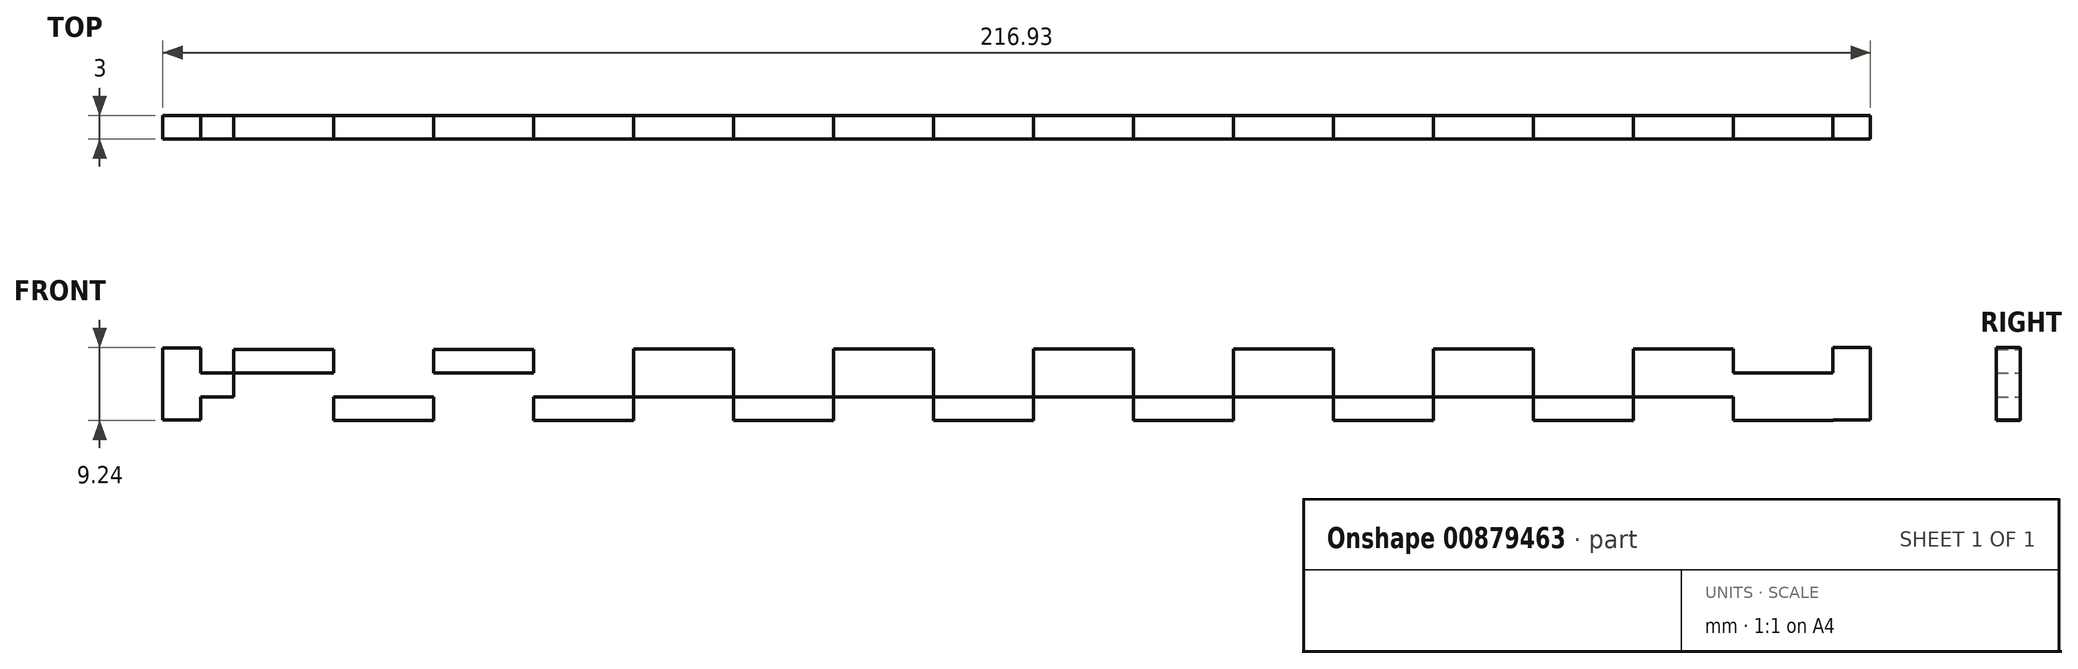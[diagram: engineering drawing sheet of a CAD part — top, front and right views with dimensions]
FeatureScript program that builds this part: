
annotation { "Feature Type Name" : "Feature", "Feature Type Description" : "" }
export const myFeature = defineFeature(function(context is Context, id is Id, definition is map)
    precondition{}
    {
        {
            var Q0;
            Q0=qCreatedBy(makeId("Front.planeOp"),FACE);
            var sketch = newSketch(context, id + "F0", { "sketchPlane" : qUnion([Q0])});
            skLineSegment(sketch, "E0.bottom", {"start": v(-108.46, 1.5) * mm, "end": v(108.46, 1.5) * mm});
            skLineSegment(sketch, "E0.top", {"start": v(-108.46, -1.5) * mm, "end": v(108.46, -1.5) * mm});
            skLineSegment(sketch, "E0.left", {"start": v(-108.46, 1.5) * mm, "end": v(-108.46, -1.5) * mm});
            skLineSegment(sketch, "E0.right", {"start": v(108.46, 1.5) * mm, "end": v(108.46, -1.5) * mm});
            skPoint(sketch, "E0.middle", {"position": v(0, 0) * mm});
            skPoint(sketch, "E1", {"position": v(-86.76, 1.5) * mm});
            skLineSegment(sketch, "E2.bottom", {"start": v(-86.76, 1.5) * mm, "end": v(-74.06, 1.5) * mm});
            skLineSegment(sketch, "E2.top", {"start": v(-86.76, -4.5) * mm, "end": v(-74.06, -4.5) * mm});
            skLineSegment(sketch, "E2.left", {"start": v(-86.76, 1.5) * mm, "end": v(-86.76, -4.5) * mm});
            skLineSegment(sketch, "E2.right", {"start": v(-74.06, 1.5) * mm, "end": v(-74.06, -4.5) * mm});
            skPoint(sketch, "E3", {"position": v(-80.4, 1.5) * mm});
            skLineSegment(sketch, "E4.1.0.0", {"start": v(-61.36, 1.5) * mm, "end": v(-48.66, 1.5) * mm});
            skLineSegment(sketch, "E4.1.0.1", {"start": v(-61.36, 1.5) * mm, "end": v(-61.36, -4.5) * mm});
            skLineSegment(sketch, "E4.1.0.2", {"start": v(-61.36, -4.5) * mm, "end": v(-48.66, -4.5) * mm});
            skPoint(sketch, "E4.1.0.3", {"position": v(-61.36, 1.5) * mm});
            skLineSegment(sketch, "E4.1.0.4", {"start": v(-48.66, 1.5) * mm, "end": v(-48.66, -4.5) * mm});
            skPoint(sketch, "E4.1.0.5", {"position": v(-55, 1.5) * mm});
            skLineSegment(sketch, "E4.2.0.0", {"start": v(-35.96, 1.5) * mm, "end": v(-23.26, 1.5) * mm});
            skLineSegment(sketch, "E4.2.0.1", {"start": v(-35.96, 1.5) * mm, "end": v(-35.96, -4.5) * mm});
            skLineSegment(sketch, "E4.2.0.2", {"start": v(-35.96, -4.5) * mm, "end": v(-23.26, -4.5) * mm});
            skPoint(sketch, "E4.2.0.3", {"position": v(-35.96, 1.5) * mm});
            skLineSegment(sketch, "E4.2.0.4", {"start": v(-23.26, 1.5) * mm, "end": v(-23.26, -4.5) * mm});
            skPoint(sketch, "E4.2.0.5", {"position": v(-29.6, 1.5) * mm});
            skLineSegment(sketch, "E4.3.0.0", {"start": v(-10.56, 1.5) * mm, "end": v(2.14, 1.5) * mm});
            skLineSegment(sketch, "E4.3.0.1", {"start": v(-10.56, 1.5) * mm, "end": v(-10.56, -4.5) * mm});
            skLineSegment(sketch, "E4.3.0.2", {"start": v(-10.56, -4.5) * mm, "end": v(2.14, -4.5) * mm});
            skPoint(sketch, "E4.3.0.3", {"position": v(-10.56, 1.5) * mm});
            skLineSegment(sketch, "E4.3.0.4", {"start": v(2.14, 1.5) * mm, "end": v(2.14, -4.5) * mm});
            skPoint(sketch, "E4.3.0.5", {"position": v(-4.2, 1.5) * mm});
            skLineSegment(sketch, "E4.4.0.0", {"start": v(14.84, 1.5) * mm, "end": v(27.54, 1.5) * mm});
            skLineSegment(sketch, "E4.4.0.1", {"start": v(14.84, 1.5) * mm, "end": v(14.84, -4.5) * mm});
            skLineSegment(sketch, "E4.4.0.2", {"start": v(14.84, -4.5) * mm, "end": v(27.54, -4.5) * mm});
            skPoint(sketch, "E4.4.0.3", {"position": v(14.84, 1.5) * mm});
            skLineSegment(sketch, "E4.4.0.4", {"start": v(27.54, 1.5) * mm, "end": v(27.54, -4.5) * mm});
            skPoint(sketch, "E4.4.0.5", {"position": v(21.2, 1.5) * mm});
            skLineSegment(sketch, "E4.5.0.0", {"start": v(40.24, 1.5) * mm, "end": v(52.94, 1.5) * mm});
            skLineSegment(sketch, "E4.5.0.1", {"start": v(40.24, 1.5) * mm, "end": v(40.24, -4.5) * mm});
            skLineSegment(sketch, "E4.5.0.2", {"start": v(40.24, -4.5) * mm, "end": v(52.94, -4.5) * mm});
            skPoint(sketch, "E4.5.0.3", {"position": v(40.24, 1.5) * mm});
            skLineSegment(sketch, "E4.5.0.4", {"start": v(52.94, 1.5) * mm, "end": v(52.94, -4.5) * mm});
            skPoint(sketch, "E4.5.0.5", {"position": v(46.6, 1.5) * mm});
            skLineSegment(sketch, "E4.6.0.0", {"start": v(65.64, 1.5) * mm, "end": v(78.34, 1.5) * mm});
            skLineSegment(sketch, "E4.6.0.1", {"start": v(65.64, 1.5) * mm, "end": v(65.64, -4.5) * mm});
            skLineSegment(sketch, "E4.6.0.2", {"start": v(65.64, -4.5) * mm, "end": v(78.34, -4.5) * mm});
            skPoint(sketch, "E4.6.0.3", {"position": v(65.64, 1.5) * mm});
            skLineSegment(sketch, "E4.6.0.4", {"start": v(78.34, 1.5) * mm, "end": v(78.34, -4.5) * mm});
            skPoint(sketch, "E4.6.0.5", {"position": v(72, 1.5) * mm});
            skLineSegment(sketch, "E4.7.0.0", {"start": v(91.04, 1.5) * mm, "end": v(103.74, 1.5) * mm});
            skLineSegment(sketch, "E4.7.0.1", {"start": v(91.04, 1.5) * mm, "end": v(91.04, -4.5) * mm});
            skLineSegment(sketch, "E4.7.0.2", {"start": v(91.04, -4.5) * mm, "end": v(103.74, -4.5) * mm});
            skPoint(sketch, "E4.7.0.3", {"position": v(91.04, 1.5) * mm});
            skLineSegment(sketch, "E4.7.0.4", {"start": v(103.74, 1.5) * mm, "end": v(103.74, -4.5) * mm});
            skPoint(sketch, "E4.7.0.5", {"position": v(97.4, 1.5) * mm});
            skLineSegment(sketch, "E4.direction1", {"start": v(-86.76, -4.5) * mm, "end": v(-61.36, -4.5) * mm, "construction": true});
            skLineSegment(sketch, "E5.bottom", {"start": v(-103.66, 4.71) * mm, "end": v(-108.46, 4.71) * mm});
            skLineSegment(sketch, "E5.top", {"start": v(-103.66, -4.46) * mm, "end": v(-108.46, -4.46) * mm});
            skLineSegment(sketch, "E5.left", {"start": v(-103.66, 4.71) * mm, "end": v(-103.66, -4.46) * mm});
            skLineSegment(sketch, "E5.right", {"start": v(-108.46, 4.71) * mm, "end": v(-108.46, -4.46) * mm});
            skLineSegment(sketch, "E6.bottom", {"start": v(108.47, 4.74) * mm, "end": v(103.67, 4.74) * mm});
            skLineSegment(sketch, "E6.top", {"start": v(108.47, -4.43) * mm, "end": v(103.67, -4.43) * mm});
            skLineSegment(sketch, "E6.left", {"start": v(108.47, 4.74) * mm, "end": v(108.47, -4.43) * mm});
            skLineSegment(sketch, "E6.right", {"start": v(103.67, 4.74) * mm, "end": v(103.67, -4.43) * mm});
            skLineSegment(sketch, "E7.bottom", {"start": v(-86.76, -1.5) * mm, "end": v(-99.46, -1.5) * mm});
            skLineSegment(sketch, "E7.top", {"start": v(-86.76, 4.5) * mm, "end": v(-99.46, 4.5) * mm});
            skLineSegment(sketch, "E7.left", {"start": v(-86.76, -1.5) * mm, "end": v(-86.76, 4.5) * mm});
            skLineSegment(sketch, "E7.right", {"start": v(-99.46, -1.5) * mm, "end": v(-99.46, 4.5) * mm});
            skPoint(sketch, "E8.1.0.0", {"position": v(-61.36, 1.59) * mm});
            skLineSegment(sketch, "E8.1.0.1", {"start": v(-61.36, 4.5) * mm, "end": v(-74.06, 4.5) * mm});
            skLineSegment(sketch, "E8.1.0.2", {"start": v(-61.36, -1.5) * mm, "end": v(-61.36, 4.5) * mm});
            skLineSegment(sketch, "E8.1.0.3", {"start": v(-74.06, -1.5) * mm, "end": v(-74.06, 4.5) * mm});
            skLineSegment(sketch, "E8.1.0.4", {"start": v(-61.36, -1.5) * mm, "end": v(-74.06, -1.5) * mm});
            skPoint(sketch, "E8.2.0.0", {"position": v(-35.96, 1.59) * mm});
            skLineSegment(sketch, "E8.2.0.1", {"start": v(-35.96, 4.59) * mm, "end": v(-48.66, 4.59) * mm});
            skLineSegment(sketch, "E8.2.0.2", {"start": v(-35.96, -1.41) * mm, "end": v(-35.96, 4.59) * mm});
            skLineSegment(sketch, "E8.2.0.3", {"start": v(-48.66, -1.41) * mm, "end": v(-48.66, 4.59) * mm});
            skLineSegment(sketch, "E8.2.0.4", {"start": v(-35.96, -1.41) * mm, "end": v(-48.66, -1.41) * mm});
            skPoint(sketch, "E8.3.0.0", {"position": v(-10.56, 1.59) * mm});
            skLineSegment(sketch, "E8.3.0.1", {"start": v(-10.56, 4.59) * mm, "end": v(-23.26, 4.59) * mm});
            skLineSegment(sketch, "E8.3.0.2", {"start": v(-10.56, -1.41) * mm, "end": v(-10.56, 4.59) * mm});
            skLineSegment(sketch, "E8.3.0.3", {"start": v(-23.26, -1.41) * mm, "end": v(-23.26, 4.59) * mm});
            skLineSegment(sketch, "E8.3.0.4", {"start": v(-10.56, -1.41) * mm, "end": v(-23.26, -1.41) * mm});
            skPoint(sketch, "E8.4.0.0", {"position": v(14.84, 1.59) * mm});
            skLineSegment(sketch, "E8.4.0.1", {"start": v(14.84, 4.59) * mm, "end": v(2.14, 4.59) * mm});
            skLineSegment(sketch, "E8.4.0.2", {"start": v(14.84, -1.41) * mm, "end": v(14.84, 4.59) * mm});
            skLineSegment(sketch, "E8.4.0.3", {"start": v(2.14, -1.41) * mm, "end": v(2.14, 4.59) * mm});
            skLineSegment(sketch, "E8.4.0.4", {"start": v(14.84, -1.41) * mm, "end": v(2.14, -1.41) * mm});
            skPoint(sketch, "E8.5.0.0", {"position": v(40.24, 1.59) * mm});
            skLineSegment(sketch, "E8.5.0.1", {"start": v(40.24, 4.59) * mm, "end": v(27.54, 4.59) * mm});
            skLineSegment(sketch, "E8.5.0.2", {"start": v(40.24, -1.41) * mm, "end": v(40.24, 4.59) * mm});
            skLineSegment(sketch, "E8.5.0.3", {"start": v(27.54, -1.41) * mm, "end": v(27.54, 4.59) * mm});
            skLineSegment(sketch, "E8.5.0.4", {"start": v(40.24, -1.41) * mm, "end": v(27.54, -1.41) * mm});
            skPoint(sketch, "E8.6.0.0", {"position": v(65.64, 1.59) * mm});
            skLineSegment(sketch, "E8.6.0.1", {"start": v(65.64, 4.59) * mm, "end": v(52.94, 4.59) * mm});
            skLineSegment(sketch, "E8.6.0.2", {"start": v(65.64, -1.41) * mm, "end": v(65.64, 4.59) * mm});
            skLineSegment(sketch, "E8.6.0.3", {"start": v(52.94, -1.41) * mm, "end": v(52.94, 4.59) * mm});
            skLineSegment(sketch, "E8.6.0.4", {"start": v(65.64, -1.41) * mm, "end": v(52.94, -1.41) * mm});
            skPoint(sketch, "E8.7.0.0", {"position": v(91.04, 1.59) * mm});
            skLineSegment(sketch, "E8.7.0.1", {"start": v(91.04, 4.59) * mm, "end": v(78.34, 4.59) * mm});
            skLineSegment(sketch, "E8.7.0.2", {"start": v(91.04, -1.41) * mm, "end": v(91.04, 4.59) * mm});
            skLineSegment(sketch, "E8.7.0.3", {"start": v(78.34, -1.41) * mm, "end": v(78.34, 4.59) * mm});
            skLineSegment(sketch, "E8.7.0.4", {"start": v(91.04, -1.41) * mm, "end": v(78.34, -1.41) * mm});
            skLineSegment(sketch, "E8.direction1", {"start": v(-99.46, -1.5) * mm, "end": v(-74.06, -1.5) * mm, "construction": true});
            skSolve(sketch);
        }
        {
            var Q0;
            {var subQ5=sQuery(id+"F0.wireOp",EDGE,"E8.7.0.1");Q0=makeQuery(id+"F0.imprint","IMPRINT",FACE,{"disambiguationData":[TD([[makeQuery(id+"F0.imprint","IMPRINT",EDGE,{"derivedFrom":subQ5}),1.0]])]});}
            var Q1;
            {var subQ5=sQuery(id+"F0.wireOp",EDGE,"E8.5.0.1");Q1=makeQuery(id+"F0.imprint","IMPRINT",FACE,{"disambiguationData":[TD([[makeQuery(id+"F0.imprint","IMPRINT",EDGE,{"derivedFrom":subQ5}),1.0]])]});}
            var Q2;
            {var subQ5=sQuery(id+"F0.wireOp",EDGE,"E8.3.0.1");Q2=makeQuery(id+"F0.imprint","IMPRINT",FACE,{"disambiguationData":[TD([[makeQuery(id+"F0.imprint","IMPRINT",EDGE,{"derivedFrom":subQ5}),1.0]])]});}
            var Q3;
            {var subQ5=sQuery(id+"F0.wireOp",EDGE,"E8.2.0.1");Q3=makeQuery(id+"F0.imprint","IMPRINT",FACE,{"disambiguationData":[TD([[makeQuery(id+"F0.imprint","IMPRINT",EDGE,{"derivedFrom":subQ5}),1.0]])]});}
            var Q4;
            {var subQ5=sQuery(id+"F0.wireOp",EDGE,"E8.1.0.1");Q4=makeQuery(id+"F0.imprint","IMPRINT",FACE,{"disambiguationData":[TD([[makeQuery(id+"F0.imprint","IMPRINT",EDGE,{"derivedFrom":subQ5}),1.0]])]});}
            var Q5;
            {var subQ5=sQuery(id+"F0.wireOp",EDGE,"E8.6.0.1");Q5=makeQuery(id+"F0.imprint","IMPRINT",FACE,{"disambiguationData":[TD([[makeQuery(id+"F0.imprint","IMPRINT",EDGE,{"derivedFrom":subQ5}),1.0]])]});}
            var Q6;
            {var subQ5=sQuery(id+"F0.wireOp",EDGE,"E7.bottom");Q6=makeQuery(id+"F0.imprint","IMPRINT",FACE,{"disambiguationData":[TD([[makeQuery(id+"F0.imprint","IMPRINT",EDGE,{"derivedFrom":subQ5}),-1.0]])]});}
            var Q7;
            {var subQ5=sQuery(id+"F0.wireOp",EDGE,"E7.top");Q7=makeQuery(id+"F0.imprint","IMPRINT",FACE,{"disambiguationData":[TD([[makeQuery(id+"F0.imprint","IMPRINT",EDGE,{"derivedFrom":subQ5}),1.0]])]});}
            var Q8;
            {var subQ5=sQuery(id+"F0.wireOp",EDGE,"E8.7.0.4");Q8=makeQuery(id+"F0.imprint","IMPRINT",FACE,{"disambiguationData":[TD([[makeQuery(id+"F0.imprint","IMPRINT",EDGE,{"derivedFrom":subQ5}),-1.0]])]});}
            var Q9;
            {var subQ0=sQuery(id+"F0.wireOp",EDGE,"E4.1.0.1");Q9=makeQuery(id+"F0.imprint","IMPRINT",FACE,{"disambiguationData":[TD([[makeQuery(id+"F0.imprint","IMPRINT",EDGE,{"derivedFrom":subQ0}),1.0]])]});}
            var Q10;
            {var subQ5=sQuery(id+"F0.wireOp",EDGE,"E8.2.0.4");Q10=makeQuery(id+"F0.imprint","IMPRINT",FACE,{"disambiguationData":[TD([[makeQuery(id+"F0.imprint","IMPRINT",EDGE,{"derivedFrom":subQ5}),1.0]])]});}
            var Q11;
            {var subQ5=sQuery(id+"F0.wireOp",EDGE,"E2.bottom");Q11=makeQuery(id+"F0.imprint","IMPRINT",FACE,{"disambiguationData":[TD([[makeQuery(id+"F0.imprint","IMPRINT",EDGE,{"derivedFrom":subQ5}),-1.0]])]});}
            var Q12;
            {var subQ5=sQuery(id+"F0.wireOp",EDGE,"E4.5.0.2");Q12=makeQuery(id+"F0.imprint","IMPRINT",FACE,{"disambiguationData":[TD([[makeQuery(id+"F0.imprint","IMPRINT",EDGE,{"derivedFrom":subQ5}),1.0]])]});}
            var Q13;
            Q13=makeQuery(id+"F0.imprint","IMPRINT",FACE,{"disambiguationData":[TD([[makeQuery(id+"F0.imprint","IMPRINT",EDGE,{"derivedFrom":sQuery(id+"F0.wireOp",EDGE,"E2.top")}),1.0]])]});
            var Q14;
            {var subQ9=sQuery(id+"F0.wireOp",EDGE,"E4.5.0.0");Q14=makeQuery(id+"F0.imprint","IMPRINT",FACE,{"disambiguationData":[TD([[makeQuery(id+"F0.imprint","IMPRINT",EDGE,{"derivedFrom":subQ9}),-1.0]])]});}
            var Q15;
            {var subQ5=sQuery(id+"F0.wireOp",EDGE,"E8.2.0.4");Q15=makeQuery(id+"F0.imprint","IMPRINT",FACE,{"disambiguationData":[TD([[makeQuery(id+"F0.imprint","IMPRINT",EDGE,{"derivedFrom":subQ5}),-1.0]])]});}
            var Q16;
            {var subQ5=sQuery(id+"F0.wireOp",EDGE,"E8.6.0.4");Q16=makeQuery(id+"F0.imprint","IMPRINT",FACE,{"disambiguationData":[TD([[makeQuery(id+"F0.imprint","IMPRINT",EDGE,{"derivedFrom":subQ5}),-1.0]])]});}
            var Q17;
            {var subQ5=sQuery(id+"F0.wireOp",EDGE,"E8.3.0.4");Q17=makeQuery(id+"F0.imprint","IMPRINT",FACE,{"disambiguationData":[TD([[makeQuery(id+"F0.imprint","IMPRINT",EDGE,{"derivedFrom":subQ5}),1.0]])]});}
            var Q18;
            {var subQ6=sQuery(id+"F0.wireOp",EDGE,"E4.1.0.0");Q18=makeQuery(id+"F0.imprint","IMPRINT",FACE,{"disambiguationData":[TD([[makeQuery(id+"F0.imprint","IMPRINT",EDGE,{"derivedFrom":subQ6}),-1.0]])]});}
            var Q19;
            {var subQ5=sQuery(id+"F0.wireOp",EDGE,"E4.6.0.0");Q19=makeQuery(id+"F0.imprint","IMPRINT",FACE,{"disambiguationData":[TD([[makeQuery(id+"F0.imprint","IMPRINT",EDGE,{"derivedFrom":subQ5}),-1.0]])]});}
            var Q20;
            {var subQ3=sQuery(id+"F0.wireOp",EDGE,"E0.top");var subQ7=sQuery(id+"F0.wireOp",EDGE,"E4.7.0.1");var subQ9=makeQuery(id+"F0.imprint","INTERSECT",VERTEX,{"derivedFrom":[subQ3,subQ7]});Q20=makeQuery(id+"F0.imprint","IMPRINT",FACE,{"disambiguationData":[TD([[makeQuery(id+"F0.imprint","IMPRINT",EDGE,{"disambiguationData":[TD([[subQ9,-1.0]])],"derivedFrom":subQ3}),1.0]])]});}
            var Q21;
            {var subQ5=sQuery(id+"F0.wireOp",EDGE,"E4.6.0.2");Q21=makeQuery(id+"F0.imprint","IMPRINT",FACE,{"disambiguationData":[TD([[makeQuery(id+"F0.imprint","IMPRINT",EDGE,{"derivedFrom":subQ5}),1.0]])]});}
            var Q22;
            {var subQ0=sQuery(id+"F0.wireOp",EDGE,"E4.7.0.2");Q22=makeQuery(id+"F0.imprint","IMPRINT",FACE,{"disambiguationData":[TD([[makeQuery(id+"F0.imprint","IMPRINT",EDGE,{"derivedFrom":subQ0}),1.0]])]});}
            var Q23;
            {var subQ5=sQuery(id+"F0.wireOp",EDGE,"E4.4.0.2");Q23=makeQuery(id+"F0.imprint","IMPRINT",FACE,{"disambiguationData":[TD([[makeQuery(id+"F0.imprint","IMPRINT",EDGE,{"derivedFrom":subQ5}),1.0]])]});}
            var Q24;
            {var subQ5=sQuery(id+"F0.wireOp",EDGE,"E8.4.0.4");Q24=makeQuery(id+"F0.imprint","IMPRINT",FACE,{"disambiguationData":[TD([[makeQuery(id+"F0.imprint","IMPRINT",EDGE,{"derivedFrom":subQ5}),1.0]])]});}
            var Q25;
            {var subQ5=sQuery(id+"F0.wireOp",EDGE,"E8.7.0.4");Q25=makeQuery(id+"F0.imprint","IMPRINT",FACE,{"disambiguationData":[TD([[makeQuery(id+"F0.imprint","IMPRINT",EDGE,{"derivedFrom":subQ5}),1.0]])]});}
            var Q26;
            {var subQ5=sQuery(id+"F0.wireOp",EDGE,"E4.4.0.0");Q26=makeQuery(id+"F0.imprint","IMPRINT",FACE,{"disambiguationData":[TD([[makeQuery(id+"F0.imprint","IMPRINT",EDGE,{"derivedFrom":subQ5}),-1.0]])]});}
            var Q27;
            {var subQ5=sQuery(id+"F0.wireOp",EDGE,"E8.5.0.4");Q27=makeQuery(id+"F0.imprint","IMPRINT",FACE,{"disambiguationData":[TD([[makeQuery(id+"F0.imprint","IMPRINT",EDGE,{"derivedFrom":subQ5}),-1.0]])]});}
            var Q28;
            {var subQ5=sQuery(id+"F0.wireOp",EDGE,"E8.4.0.4");Q28=makeQuery(id+"F0.imprint","IMPRINT",FACE,{"disambiguationData":[TD([[makeQuery(id+"F0.imprint","IMPRINT",EDGE,{"derivedFrom":subQ5}),-1.0]])]});}
            var Q29;
            {var subQ9=sQuery(id+"F0.wireOp",EDGE,"E4.2.0.0");Q29=makeQuery(id+"F0.imprint","IMPRINT",FACE,{"disambiguationData":[TD([[makeQuery(id+"F0.imprint","IMPRINT",EDGE,{"derivedFrom":subQ9}),-1.0]])]});}
            var Q30;
            {var subQ5=sQuery(id+"F0.wireOp",EDGE,"E8.6.0.4");Q30=makeQuery(id+"F0.imprint","IMPRINT",FACE,{"disambiguationData":[TD([[makeQuery(id+"F0.imprint","IMPRINT",EDGE,{"derivedFrom":subQ5}),1.0]])]});}
            var Q31;
            {var subQ5=sQuery(id+"F0.wireOp",EDGE,"E4.2.0.2");Q31=makeQuery(id+"F0.imprint","IMPRINT",FACE,{"disambiguationData":[TD([[makeQuery(id+"F0.imprint","IMPRINT",EDGE,{"derivedFrom":subQ5}),1.0]])]});}
            var Q32;
            {var subQ5=sQuery(id+"F0.wireOp",EDGE,"E8.4.0.1");Q32=makeQuery(id+"F0.imprint","IMPRINT",FACE,{"disambiguationData":[TD([[makeQuery(id+"F0.imprint","IMPRINT",EDGE,{"derivedFrom":subQ5}),1.0]])]});}
            var Q33;
            {var subQ5=sQuery(id+"F0.wireOp",EDGE,"E8.3.0.4");Q33=makeQuery(id+"F0.imprint","IMPRINT",FACE,{"disambiguationData":[TD([[makeQuery(id+"F0.imprint","IMPRINT",EDGE,{"derivedFrom":subQ5}),-1.0]])]});}
            var Q34;
            {var subQ5=sQuery(id+"F0.wireOp",EDGE,"E8.1.0.4");Q34=makeQuery(id+"F0.imprint","IMPRINT",FACE,{"disambiguationData":[TD([[makeQuery(id+"F0.imprint","IMPRINT",EDGE,{"derivedFrom":subQ5}),-1.0]])]});}
            var Q35;
            {var subQ5=sQuery(id+"F0.wireOp",EDGE,"E8.5.0.4");Q35=makeQuery(id+"F0.imprint","IMPRINT",FACE,{"disambiguationData":[TD([[makeQuery(id+"F0.imprint","IMPRINT",EDGE,{"derivedFrom":subQ5}),1.0]])]});}
            var Q36;
            {var subQ0=sQuery(id+"F0.wireOp",EDGE,"E5.right");var subQ1=sQuery(id+"F0.wireOp",EDGE,"E0.bottom");var subQ2=makeQuery(id+"F0.imprint","INTERSECT",VERTEX,{"derivedFrom":[subQ1,subQ0]});Q36=makeQuery(id+"F0.imprint","IMPRINT",FACE,{"disambiguationData":[TD([[makeQuery(id+"F0.imprint","IMPRINT",EDGE,{"disambiguationData":[TD([[subQ2,-1.0]])],"derivedFrom":subQ1}),-1.0]])]});}
            var Q37;
            {var subQ5=sQuery(id+"F0.wireOp",EDGE,"E5.top");Q37=makeQuery(id+"F0.imprint","IMPRINT",FACE,{"disambiguationData":[TD([[makeQuery(id+"F0.imprint","IMPRINT",EDGE,{"derivedFrom":subQ5}),-1.0]])]});}
            var Q38;
            {var subQ5=sQuery(id+"F0.wireOp",EDGE,"E4.3.0.2");Q38=makeQuery(id+"F0.imprint","IMPRINT",FACE,{"disambiguationData":[TD([[makeQuery(id+"F0.imprint","IMPRINT",EDGE,{"derivedFrom":subQ5}),1.0]])]});}
            var Q39;
            {var subQ0=sQuery(id+"F0.wireOp",EDGE,"E5.left");var subQ1=sQuery(id+"F0.wireOp",EDGE,"E0.bottom");var subQ2=makeQuery(id+"F0.imprint","INTERSECT",VERTEX,{"derivedFrom":[subQ1,subQ0]});Q39=makeQuery(id+"F0.imprint","IMPRINT",FACE,{"disambiguationData":[TD([[makeQuery(id+"F0.imprint","IMPRINT",EDGE,{"disambiguationData":[TD([[subQ2,-1.0]])],"derivedFrom":subQ1}),-1.0]])]});}
            var Q40;
            {var subQ9=sQuery(id+"F0.wireOp",EDGE,"E4.3.0.0");Q40=makeQuery(id+"F0.imprint","IMPRINT",FACE,{"disambiguationData":[TD([[makeQuery(id+"F0.imprint","IMPRINT",EDGE,{"derivedFrom":subQ9}),-1.0]])]});}
            var Q41;
            {var subQ5=sQuery(id+"F0.wireOp",EDGE,"E5.bottom");Q41=makeQuery(id+"F0.imprint","IMPRINT",FACE,{"disambiguationData":[TD([[makeQuery(id+"F0.imprint","IMPRINT",EDGE,{"derivedFrom":subQ5}),1.0]])]});}
            var Q42;
            {var subQ0=sQuery(id+"F0.wireOp",EDGE,"E0.right");Q42=makeQuery(id+"F0.imprint","IMPRINT",FACE,{"disambiguationData":[TD([[makeQuery(id+"F0.imprint","IMPRINT",EDGE,{"derivedFrom":subQ0}),1.0]])]});}
            var Q43;
            {var subQ0=sQuery(id+"F0.wireOp",EDGE,"E0.right");Q43=makeQuery(id+"F0.imprint","IMPRINT",FACE,{"disambiguationData":[TD([[makeQuery(id+"F0.imprint","IMPRINT",EDGE,{"derivedFrom":subQ0}),-1.0]])]});}
            var Q44;
            {var subQ0=sQuery(id+"F0.wireOp",EDGE,"E6.right");var subQ1=sQuery(id+"F0.wireOp",EDGE,"E0.top");var subQ2=makeQuery(id+"F0.imprint","INTERSECT",VERTEX,{"derivedFrom":[subQ1,subQ0]});Q44=makeQuery(id+"F0.imprint","IMPRINT",FACE,{"disambiguationData":[TD([[makeQuery(id+"F0.imprint","IMPRINT",EDGE,{"disambiguationData":[TD([[subQ2,-1.0]])],"derivedFrom":subQ1}),1.0]])]});}
            var Q45;
            {var subQ0=sQuery(id+"F0.wireOp",EDGE,"E6.right");var subQ1=sQuery(id+"F0.wireOp",EDGE,"E0.top");var subQ2=makeQuery(id+"F0.imprint","INTERSECT",VERTEX,{"derivedFrom":[subQ1,subQ0]});Q45=makeQuery(id+"F0.imprint","IMPRINT",FACE,{"disambiguationData":[TD([[makeQuery(id+"F0.imprint","IMPRINT",EDGE,{"disambiguationData":[TD([[subQ2,-1.0]])],"derivedFrom":subQ1}),-1.0]])]});}
            extrude(context, id + "F1", {"entities" : qUnion([Q0, Q1, Q2, Q3, Q4, Q5, Q6, Q7, Q8, Q9, Q10, Q11, Q12, Q13, Q14, Q15, Q16, Q17, Q18, Q19, Q20, Q21, Q22, Q23, Q24, Q25, Q26, Q27, Q28, Q29, Q30, Q31, Q32, Q33, Q34, Q35, Q36, Q37, Q38, Q39, Q40, Q41, Q42, Q43, Q44, Q45]), "depth" : 3 * mm, "offsetDistance" : 25 * mm});
        }
    });
